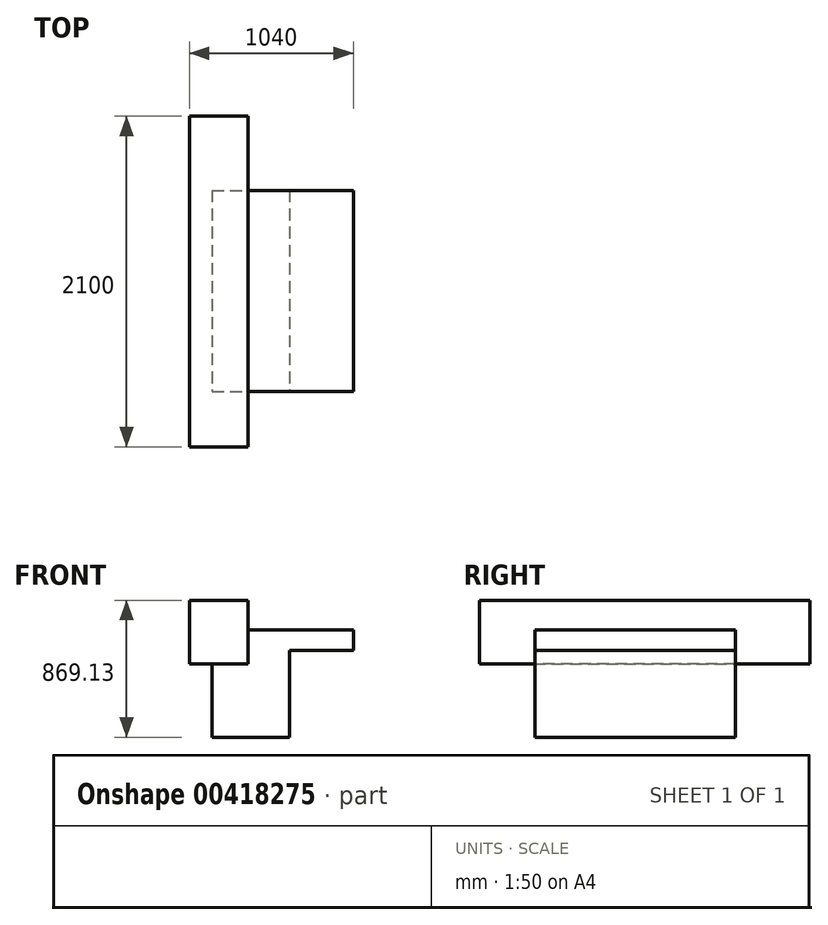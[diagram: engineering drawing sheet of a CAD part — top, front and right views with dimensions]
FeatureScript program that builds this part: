
annotation { "Feature Type Name" : "Feature", "Feature Type Description" : "" }
export const myFeature = defineFeature(function(context is Context, id is Id, definition is map)
    precondition{}
    {
        {
            var Q0;
            Q0=qCreatedBy(makeId("Front.planeOp"),FACE);
            var sketch = newSketch(context, id + "F0", { "sketchPlane" : qUnion([Q0])});
            skLineSegment(sketch, "E0.bottom", {"start": v(0, 0) * mm, "end": v(370, 0) * mm});
            skLineSegment(sketch, "E0.top", {"start": v(0, 402) * mm, "end": v(370, 402) * mm});
            skLineSegment(sketch, "E0.left", {"start": v(0, 0) * mm, "end": v(0, 402) * mm});
            skLineSegment(sketch, "E0.right", {"start": v(370, 0) * mm, "end": v(370, 402) * mm});
            skLineSegment(sketch, "E1.bottom", {"start": v(370, 82.87) * mm, "end": v(1040, 82.87) * mm});
            skLineSegment(sketch, "E1.top", {"start": v(370, 212.87) * mm, "end": v(1040, 212.87) * mm});
            skLineSegment(sketch, "E1.left", {"start": v(370, 82.87) * mm, "end": v(370, 212.87) * mm});
            skLineSegment(sketch, "E1.right", {"start": v(1040, 82.87) * mm, "end": v(1040, 212.87) * mm});
            skSolve(sketch);
        }
        {
            var Q0;
            {var subQ1=sQuery(id+"F0.wireOp",EDGE,"E0.bottom");Q0=makeQuery(id+"F0.imprint","IMPRINT",FACE,{"disambiguationData":[TD([[makeQuery(id+"F0.imprint","IMPRINT",EDGE,{"derivedFrom":subQ1}),1.0]])]});}
            var Q1;
            Q1=makeQuery(id+"F0.imprint","IMPRINT",FACE,{"disambiguationData":[TD([[makeQuery(id+"F0.imprint","IMPRINT",EDGE,{"derivedFrom":sQuery(id+"F0.wireOp",EDGE,"E1.bottom")}),1.0]])]});
            extrude(context, id + "F1", {"entities" : qUnion([Q0, Q1]), "depth" : 2100 * mm});
        }
        {
            var Q0;
            Q0=makeQuery(id+"F1.opExtrude","SWEPT_FACE",FACE,{"disambiguationData":[OSD([sQuery(id+"F0.wireOp",EDGE,"E1.bottom")])]});
            var sketch = newSketch(context, id + "F2", { "sketchPlane" : qUnion([Q0])});
            skLineSegment(sketch, "E2.bottom", {"start": v(143.5, 471.4) * mm, "end": v(634.47, 471.4) * mm});
            skLineSegment(sketch, "E2.top", {"start": v(143.5, 1746.8) * mm, "end": v(634.47, 1746.8) * mm});
            skLineSegment(sketch, "E2.left", {"start": v(143.5, 471.4) * mm, "end": v(143.5, 1746.8) * mm});
            skLineSegment(sketch, "E2.right", {"start": v(634.47, 471.4) * mm, "end": v(634.47, 1746.8) * mm});
            skSolve(sketch);
        }
        {
            var Q0;
            Q0 = qSketchRegion(id + "F2", true);
            extrude(context, id + "F3", {"entities" : qUnion([Q0]), "operationType" : NewBodyOperationType.ADD, "depth" : 550 * mm});
        }
        {
            var Q0;
            Q0=makeQuery(id+"F1.opExtrude","SWEPT_FACE",FACE,{"disambiguationData":[OSD([sQuery(id+"F0.wireOp",EDGE,"E1.bottom")])]});
            var sketch = newSketch(context, id + "F4", { "sketchPlane" : qUnion([Q0])});
            skPoint(sketch, "E3.oppositeSnap0", {"position": v(502.23, 471.4) * mm});
            skLineSegment(sketch, "E3.bottom", {"start": v(370, 0) * mm, "end": v(1040, 0) * mm});
            skLineSegment(sketch, "E3.top", {"start": v(370, 471.4) * mm, "end": v(1040, 471.4) * mm});
            skLineSegment(sketch, "E3.left", {"start": v(370, 0) * mm, "end": v(370, 471.4) * mm});
            skLineSegment(sketch, "E3.right", {"start": v(1040, 0) * mm, "end": v(1040, 471.4) * mm});
            skLineSegment(sketch, "E4.bottom", {"start": v(370, 1746.8) * mm, "end": v(1040, 1746.8) * mm});
            skLineSegment(sketch, "E4.top", {"start": v(370, 2100) * mm, "end": v(1040, 2100) * mm});
            skLineSegment(sketch, "E4.left", {"start": v(370, 1746.8) * mm, "end": v(370, 2100) * mm});
            skLineSegment(sketch, "E4.right", {"start": v(1040, 1746.8) * mm, "end": v(1040, 2100) * mm});
            skSolve(sketch);
        }
        {
            var Q0;
            Q0 = qSketchRegion(id + "F4", true);
            extrude(context, id + "F5", {"entities" : qUnion([Q0]), "operationType" : NewBodyOperationType.REMOVE, "oppositeDirection" : true, "depth" : 500 * mm});
        }
    });
